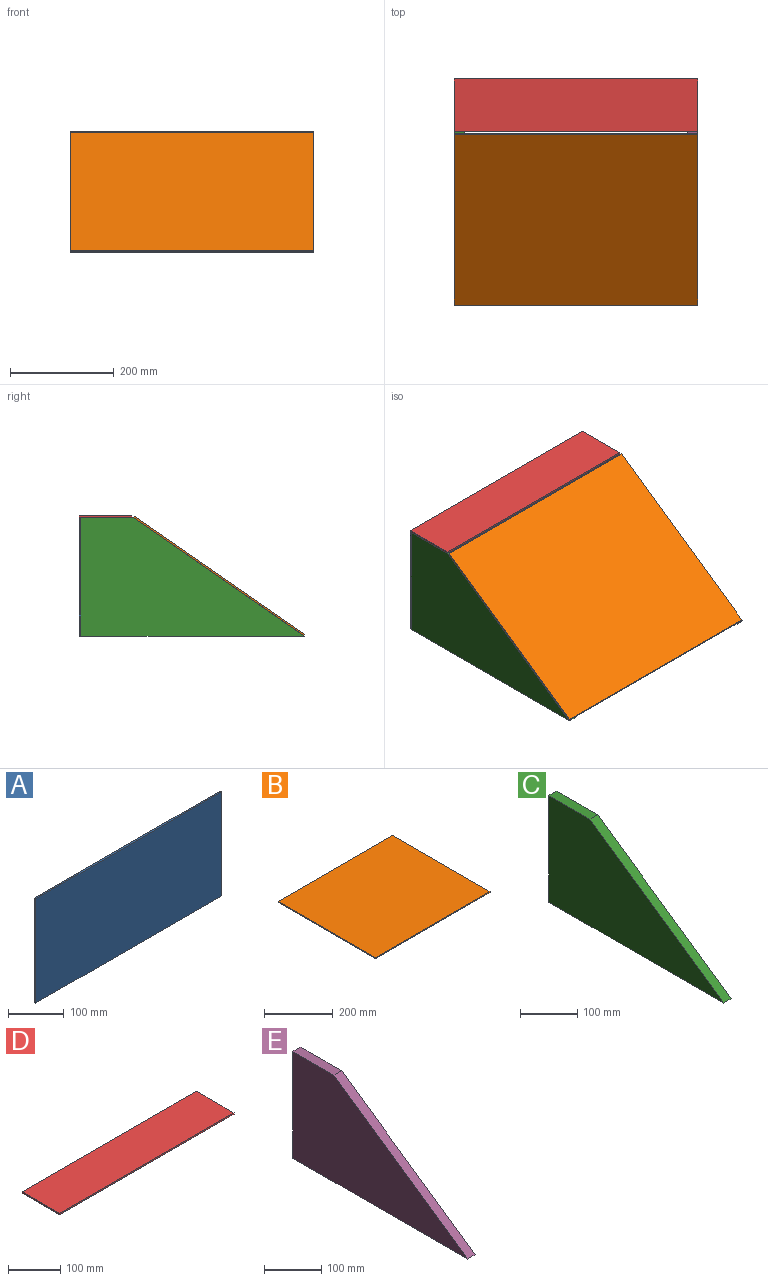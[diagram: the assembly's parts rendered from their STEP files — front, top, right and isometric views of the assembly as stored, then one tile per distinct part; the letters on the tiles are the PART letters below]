
ASSEMBLY  parts=5 mates=4
PART A: 6 faces, bbox 469.9x3.2x228.6 mm
  f0: plane 469.9x3.18mm, normal (0,0,-1), area 1491.9mm2, adj f1,f3,f4,f5
  f1: plane 228.6x3.18mm, normal (1,0,0), area 725.8mm2, adj f0,f2,f4,f5
  f2: plane 469.9x3.18mm, normal (0,0,1), area 1491.9mm2, adj f1,f3,f4,f5
  f3: plane 228.6x3.18mm, normal (-1,0,0), area 725.8mm2, adj f0,f2,f4,f5
  f4: plane 469.9x228.6mm, normal (0,1,0), area 107419.1mm2, adj f0,f1,f2,f3
  f5: plane 469.9x228.6mm, normal (0,-1,0), area 107419.1mm2, adj f0,f1,f2,f3
PART B: 6 faces, bbox 469.9x400.1x3.2 mm
  f0: plane 400.05x3.18mm, normal (-1,0,0), area 1270.2mm2, adj f1,f3,f4,f5
  f1: plane 469.9x3.18mm, normal (0,-1,0), area 1491.9mm2, adj f0,f2,f4,f5
  f2: plane 400.05x3.18mm, normal (1,0,0), area 1270.2mm2, adj f1,f3,f4,f5
  f3: plane 469.9x3.18mm, normal (0,1,0), area 1491.9mm2, adj f0,f2,f4,f5
  f4: plane 469.9x400.05mm, normal (0,0,1), area 187983.5mm2, adj f0,f1,f2,f3
  f5: plane 469.9x400.05mm, normal (0,0,-1), area 187983.5mm2, adj f0,f1,f2,f3
PART C: 6 faces, bbox 19.1x431.8x228.6 mm
  f0: plane 431.8x19.05mm, normal (0,0,-1), area 8225.8mm2, adj f1,f3,f4,f5
  f1: plane 330.2x228.6mm, normal (0,-0.57,0.82), area 7650.7mm2, adj f0,f2,f4,f5
  f2: plane 101.6x19.05mm, normal (0,0,1), area 1935.5mm2, adj f1,f3,f4,f5
  f3: plane 228.6x19.05mm, normal (0,1,0), area 4354.8mm2, adj f0,f2,f4,f5
  f4: plane 431.8x228.6mm, normal (1,0,0), area 60967.6mm2, adj f0,f1,f2,f3
  f5: plane 431.8x228.6mm, normal (-1,0,0), area 60967.6mm2, adj f0,f1,f2,f3
PART D: 6 faces, bbox 469.9x101.6x3.2 mm
  f0: plane 469.9x3.18mm, normal (0,-1,0), area 1491.9mm2, adj f1,f3,f4,f5
  f1: plane 101.6x3.18mm, normal (1,0,0), area 322.6mm2, adj f0,f2,f4,f5
  f2: plane 469.9x3.18mm, normal (0,1,0), area 1491.9mm2, adj f1,f3,f4,f5
  f3: plane 101.6x3.18mm, normal (-1,0,0), area 322.6mm2, adj f0,f2,f4,f5
  f4: plane 469.9x101.6mm, normal (0,0,1), area 47741.8mm2, adj f0,f1,f2,f3
  f5: plane 469.9x101.6mm, normal (0,0,-1), area 47741.8mm2, adj f0,f1,f2,f3
PART E: 6 faces, bbox 19.1x431.8x228.6 mm
  f0: plane 431.8x19.05mm, normal (0,0,-1), area 8225.8mm2, adj f1,f3,f4,f5
  f1: plane 228.6x19.05mm, normal (0,1,0), area 4354.8mm2, adj f0,f2,f4,f5
  f2: plane 101.6x19.05mm, normal (0,0,1), area 1935.5mm2, adj f1,f3,f4,f5
  f3: plane 330.2x228.6mm, normal (0,-0.57,0.82), area 7650.7mm2, adj f0,f2,f4,f5
  f4: plane 431.8x228.6mm, normal (-1,0,0), area 60967.6mm2, adj f0,f1,f2,f3
  f5: plane 431.8x228.6mm, normal (1,0,0), area 60967.6mm2, adj f0,f1,f2,f3
PLACE A t=(-225.42,215.9,0)mm
PLACE B rot(axis=(1,0,0),34.7deg) t=(-460.38,-214.62,0.89)mm
PLACE C t=(-225.42,215.9,0)mm
PLACE D t=(-225.42,215.9,0)mm
PLACE E t=(-225.42,215.9,0)mm
MATE fastened A.f5 <-> E.f1  axis (0,-1,0) through (9.53,215.9,114.3)mm
MATE fastened D.f5 <-> A.f2  axis (0,0,1) through (9.52,219.08,228.6)mm
MATE fastened E.f0 <-> C.f0  axis (0,0,-1) through (0,0,0)mm
MATE fastened C.f1 <-> B.f5  axis (0,-0.57,0.82) through (-460.38,114.3,228.6)mm
